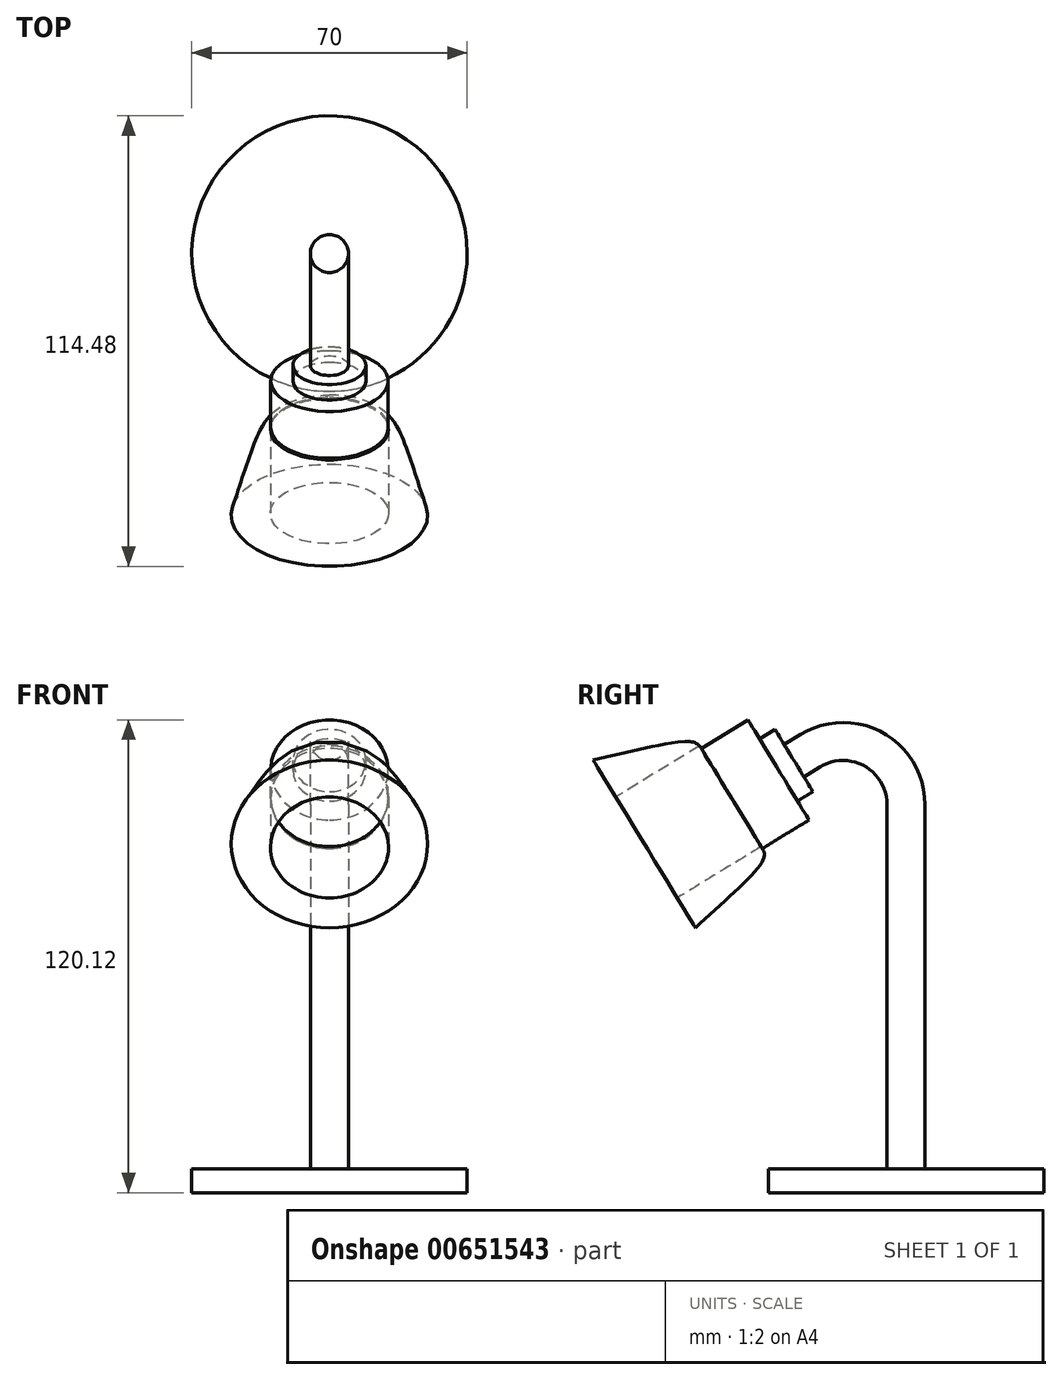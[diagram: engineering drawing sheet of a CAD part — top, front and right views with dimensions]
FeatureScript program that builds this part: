
annotation { "Feature Type Name" : "Feature", "Feature Type Description" : "" }
export const myFeature = defineFeature(function(context is Context, id is Id, definition is map)
    precondition{}
    {
        {
            var Q0;
            Q0=qCreatedBy(makeId("Top.planeOp"),FACE);
            var sketch = newSketch(context, id + "F0", { "sketchPlane" : qUnion([Q0])});
            skCircle(sketch, "E0", {"center": v(0, 0) * mm, "radius": 35 * mm});
            skSolve(sketch);
        }
        {
            var Q0;
            Q0=makeQuery(id+"F0.imprint","IMPRINT",FACE,{"disambiguationData":[TD([[makeQuery(id+"F0.imprint","IMPRINT",EDGE,{"derivedFrom":sQuery(id+"F0.wireOp",EDGE,"E0")}),1.0]])]});
            extrude(context, id + "F1", {"entities" : qUnion([Q0]), "depth" : 6 * mm, "offsetDistance" : 25 * mm});
        }
        {
            var Q0;
            Q0=makeQuery(id+"F1.opExtrude","CAP_FACE",FACE,{"disambiguationData":[OSD([sQuery(id+"F0.wireOp",EDGE,"E0")])],"isStart":false});
            var sketch = newSketch(context, id + "F2", { "sketchPlane" : qUnion([Q0])});
            skCircle(sketch, "E1", {"center": v(0, 0) * mm, "radius": 4.83 * mm});
            skSolve(sketch);
        }
        {
            var Q0;
            Q0 = qSketchRegion(id + "F2", true);
            extrude(context, id + "F3", {"entities" : qUnion([Q0]), "operationType" : NewBodyOperationType.ADD, "depth" : 78 * mm, "offsetDistance" : 25 * mm});
        }
        {
            var Q0;
            Q0=qCreatedBy(makeId("Right.planeOp"),FACE);
            var sketch = newSketch(context, id + "F4", { "sketchPlane" : qUnion([Q0])});
            skLineSegment(sketch, "E2", {"start": v(0, 78.3) * mm, "end": v(0, 98.61) * mm});
            skArc(sketch, "E3", {"start": v(0, 98.61) * mm, "mid": v(-8.18, 112.59) * mm, "end": v(-24.37, 112.3) * mm});
            skSolve(sketch);
        }
        {
            var Q0;
            Q0=makeQuery(id+"F3.opExtrude","CAP_FACE",FACE,{"disambiguationData":[OSD([sQuery(id+"F2.wireOp",EDGE,"E1")])],"isStart":false});
            var sketch = newSketch(context, id + "F5", { "sketchPlane" : qUnion([Q0])});
            skCircle(sketch, "E4", {"center": v(5.82, -8.11) * mm, "radius": 9.99 * mm});
            skSolve(sketch);
        }
        {
            var Q0;
            Q0=makeQuery(id+"F5.imprint","IMPRINT",FACE,{"disambiguationData":[TD([[makeQuery(id+"F5.imprint","IMPRINT",EDGE,{"derivedFrom":makeQuery(id+"F3.opExtrude","CAP_EDGE",EDGE,{"disambiguationData":[OSD([sQuery(id+"F2.wireOp",EDGE,"E1")])],"isStart":false})}),1.0]])]});
            var Q1;
            Q1=makeQuery(id+"F3.opExtrude","CAP_EDGE",EDGE,{"disambiguationData":[OSD([sQuery(id+"F2.wireOp",EDGE,"E1")])],"isStart":false});
            var Q2;
            Q2=sQuery(id+"F4.wireOp",EDGE,"E2");
            var Q3;
            Q3=sQuery(id+"F4.wireOp",EDGE,"E3");
            var Q4;
            Q4 = qConstructionFilter(qBodyType(qCreatedBy(id + "F4" ,EDGE), BodyType.WIRE), ConstructionObject.NO);
            sweep(context, id + "F6", {"operationType" : NewBodyOperationType.ADD, "profiles" : qUnion([Q0]), "surfaceProfiles" : qUnion([Q1, Q2, Q3]), "path" : qUnion([Q4])});
        }
        {
            var Q0;
            Q0=makeQuery(id+"F6.opSweep","CAP_FACE",FACE,{"disambiguationData":[OSD([sQuery(id+"F2.wireOp",EDGE,"E1"),sQuery(id+"F4.wireOp",VERTEX,"E3.end")])],"isStart":false});
            extrude(context, id + "F7", {"entities" : qUnion([Q0]), "operationType" : NewBodyOperationType.ADD, "depth" : 4.8 * mm, "offsetDistance" : 25 * mm});
        }
        {
            var Q0;
            Q0=makeQuery(id+"F7.opExtrude","CAP_FACE",FACE,{"disambiguationData":[OSD([sQuery(id+"F2.wireOp",EDGE,"E1"),sQuery(id+"F4.wireOp",VERTEX,"E3.end")])],"isStart":false});
            var sketch = newSketch(context, id + "F8", { "sketchPlane" : qUnion([Q0])});
            skCircle(sketch, "E5", {"center": v(0, 108.56) * mm, "radius": 9.26 * mm});
            skSolve(sketch);
        }
        {
            var Q0;
            Q0=makeQuery(id+"F8.imprint","IMPRINT",FACE,{"disambiguationData":[TD([[makeQuery(id+"F8.imprint","IMPRINT",EDGE,{"derivedFrom":sQuery(id+"F8.wireOp",EDGE,"E5")}),1.0]])]});
            var Q1;
            Q1=makeQuery(id+"F8.imprint","IMPRINT",FACE,{"disambiguationData":[TD([[makeQuery(id+"F8.imprint","IMPRINT",EDGE,{"derivedFrom":makeQuery(id+"F7.opExtrude","CAP_EDGE",EDGE,{"disambiguationData":[OSD([sQuery(id+"F2.wireOp",EDGE,"E1"),sQuery(id+"F4.wireOp",VERTEX,"E3.end")])],"isStart":false})}),1.0]])]});
            extrude(context, id + "F9", {"entities" : qUnion([Q0, Q1]), "operationType" : NewBodyOperationType.ADD, "depth" : 4.6 * mm, "offsetDistance" : 25 * mm});
        }
        {
            var Q0;
            Q0=makeQuery(id+"F9.opExtrude","CAP_FACE",FACE,{"disambiguationData":[OSD([sQuery(id+"F8.wireOp",EDGE,"E5")])],"isStart":false});
            var sketch = newSketch(context, id + "F10", { "sketchPlane" : qUnion([Q0])});
            skCircle(sketch, "E6", {"center": v(0, 108.56) * mm, "radius": 14.9 * mm});
            skSolve(sketch);
        }
        {
            var Q0;
            Q0=makeQuery(id+"F10.imprint","IMPRINT",FACE,{"disambiguationData":[TD([[makeQuery(id+"F10.imprint","IMPRINT",EDGE,{"derivedFrom":sQuery(id+"F10.wireOp",EDGE,"E6")}),1.0]])]});
            var Q1;
            Q1=makeQuery(id+"F10.imprint","IMPRINT",FACE,{"disambiguationData":[TD([[makeQuery(id+"F10.imprint","IMPRINT",EDGE,{"derivedFrom":makeQuery(id+"F9.opExtrude","CAP_EDGE",EDGE,{"disambiguationData":[OSD([sQuery(id+"F8.wireOp",EDGE,"E5")])],"isStart":false})}),1.0]])]});
            extrude(context, id + "F11", {"entities" : qUnion([Q0, Q1]), "operationType" : NewBodyOperationType.ADD, "depth" : 13.9 * mm, "offsetDistance" : 25 * mm});
        }
        {
            var Q0;
            Q0=makeQuery(id+"F11.opExtrude","CAP_FACE",FACE,{"disambiguationData":[OSD([sQuery(id+"F10.wireOp",EDGE,"E6")])],"isStart":false});
            var sketch = newSketch(context, id + "F12", { "sketchPlane" : qUnion([Q0])});
            skCircle(sketch, "E7", {"center": v(0, 108.56) * mm, "radius": 14.98 * mm});
            skSolve(sketch);
        }
        {
            var Q0;
            Q0=makeQuery(id+"F12.imprint","IMPRINT",FACE,{"disambiguationData":[TD([[makeQuery(id+"F12.imprint","IMPRINT",EDGE,{"derivedFrom":makeQuery(id+"F11.opExtrude","CAP_EDGE",EDGE,{"disambiguationData":[OSD([sQuery(id+"F10.wireOp",EDGE,"E6")])],"isStart":false})}),1.0]])]});
            cPlane(context, id + "F13", {"entities" : qUnion([Q0]), "cplaneType" : CPlaneType.OFFSET, "offset" : 25 * mm, "width" : 150 * mm, "height" : 150 * mm});
        }
        {
            var Q0;
            Q0=qCreatedBy(id+"F13.planeOp",FACE);
            var sketch = newSketch(context, id + "F14", { "sketchPlane" : qUnion([Q0])});
            skCircle(sketch, "E8", {"center": v(0, 110.26) * mm, "radius": 24.94 * mm});
            skSolve(sketch);
        }
        {
            var Q0;
            Q0=makeQuery(id+"F12.imprint","IMPRINT",FACE,{"disambiguationData":[TD([[makeQuery(id+"F12.imprint","IMPRINT",EDGE,{"derivedFrom":makeQuery(id+"F11.opExtrude","CAP_EDGE",EDGE,{"disambiguationData":[OSD([sQuery(id+"F10.wireOp",EDGE,"E6")])],"isStart":false})}),1.0]])]});
            var Q1;
            Q1=makeQuery(id+"F14.imprint","IMPRINT",FACE,{"disambiguationData":[TD([[makeQuery(id+"F14.imprint","IMPRINT",EDGE,{"derivedFrom":sQuery(id+"F14.wireOp",EDGE,"E8")}),1.0]])]});
            loft(context, id + "F15", {"startCondition" : LoftEndDerivativeType.MATCH_CURVATURE, "startMagnitude" : 1, "sheetProfilesArray" : [{ "sheetProfileEntities" : qUnion([Q0]) }, { "sheetProfileEntities" : qUnion([Q1]) }]});
        }
        {
            var Q0;
            Q0=qCreatedBy(id+"F13.planeOp",FACE);
            var sketch = newSketch(context, id + "F16", { "sketchPlane" : qUnion([Q0])});
            skCircle(sketch, "E9", {"center": v(0, 109.21) * mm, "radius": 17.82 * mm});
            skSolve(sketch);
        }
        {
            var Q0;
            Q0=sQuery(id+"F16.wireOp",VERTEX,"E9.center");
            var Q1;
            Q1=makeQuery(id+"F15.opLoft","SWEPT_BODY",BODY,{"disambiguationData":[OSD([makeQuery(id+"F12.imprint","IMPRINT",FACE,{"disambiguationData":[TD([[makeQuery(id+"F12.imprint","IMPRINT",EDGE,{"derivedFrom":makeQuery(id+"F11.opExtrude","CAP_EDGE",EDGE,{"disambiguationData":[OSD([sQuery(id+"F10.wireOp",EDGE,"E6")])],"isStart":false})}),1.0]])]}),makeQuery(id+"F14.imprint","IMPRINT",FACE,{"disambiguationData":[TD([[makeQuery(id+"F14.imprint","IMPRINT",EDGE,{"derivedFrom":sQuery(id+"F14.wireOp",EDGE,"E8")}),1.0]])]})])]});
            hole(context, id + "F17", {"style" : HoleStyle.SIMPLE, "endStyle" : HoleEndStyle.THROUGH, "holeDiameter" : 30 * mm, "majorDiameter" : 5 * mm, "isTappedThrough" : true, "tappedDepth" : 12 * mm, "tapClearance" : 3, "locations" : qUnion([Q0]), "scope" : qUnion([Q1])});
        }
    });
